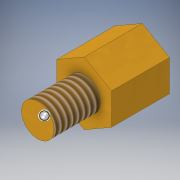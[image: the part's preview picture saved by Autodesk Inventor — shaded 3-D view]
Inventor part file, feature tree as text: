
AUTODESK INVENTOR PART (.ipt)
format: ipt  version: 2019 (Build 230136000, 136)  size: 142,848 bytes
history: native  units: mm
features: other x6, extrude x2, sketch x2, hole x1, thread x1
ambient origin geometry x8: Origin, YZ Plane, XZ Plane, XY Plane, X Axis, Y Axis, Z Axis, Center Point
bodies: Solid1 (feature_tree)
feature tree (12):
  other  "Table"
  other  "Spacer-M3-05"
  other  "Spacer-M3-10"
  other  "Spacer-M3-15"
  other  "Spacer-M3-20"
  other  "Spacer-M3-25"
  extrude  "Hexagon1"  Depth=5.0mm TaperAngle=0.0deg
  hole  "Hole1"  [1 undecoded]
  extrude  "Extrusion2"  TaperAngle=0.0deg  [1 undecoded]
  thread  "Thread3"  [1 undecoded]
  sketch  "Sketch1"  dims[d0=5.427093mm d1=5.0mm d2=0.0mm]
  sketch  "Sketch2"  dims[d27=10.0mm d28=10.0mm d5=2.459mm d6=4.0mm d7=4.4mm d8=2.0mm d9=90.0deg d10=4.5mm d11=0.0mm d13=4.0mm d14=0.0mm d19=0.0mm d20=4.7mm d21=2.713546mm d22=2.8mm d25=10.0mm d26=0.0mm]
note: 3 required parameter values undecoded (feature->parameter linkage not recoverable at this tier; creation-order binding heuristic only, values carry confidence <= 0.55)
